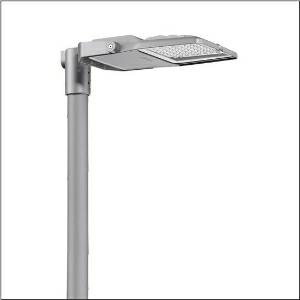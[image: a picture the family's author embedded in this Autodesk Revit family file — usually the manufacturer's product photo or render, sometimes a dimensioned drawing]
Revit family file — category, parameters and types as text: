
# Revit family: floodlight_fl_21_iq_mini___pl43_5xa7771b2a3a_6d21
name_source: partatom
category: Lighting Fixtures
units: mm (PartAtom-declared; Revit-internal decimal feet)

## family parameters
Cut with Voids When Loaded = No
Host = Face
Light Source = No
Part Type = Normal
Room Calculation Point = No
Round Connector Dimension = Use Diameter
Shared = No

## types (1)
- --- (1 x LED, 6400 lm, 45.5 W, 3000K)
    Apparent Load = 46 VA
    CIE Flux Codes = 27 78 99 100 100
    Color Rendering = 70
    Color Temperature = 3000K
    Default Elevation = 1800 mm
    Description = Floodlight FL 21 iQ mini, floodlight, primary light control with lens, of PMMA, primary optical cover: protective disc, of toughened safety glass, transparent, light distribution: PL43, light emission: direct distribution, installation type: surface-mounted, LED, High Power LED, rated luminous flux: 6.400lm, luminous efficacy: 141lm/W, light colour: 730, colour temperature: 3000K, control gear: iQ Comfort/DALI, control: Auto-Match, Temp-Guard, Lumen-Switch, Night-Set, Smart-Wire, Light-Fading, Desk-Remote (wireless, voltage-free reading and setting of iQ features in the workshop via application-optimized NFC function/RFID function), optimised constant luminous flux control (CLO 2.0), with terminal, 6-pole, mains connection: 220..240V, AC, 50/60Hz, start of lifetime: 46W, end of service life: 48W, reduction: 22W, luminaire housing, of diecast aluminium, powder-coated, Siteco® metallic grey (DB 702S), corrosivity category C5 mid according to DIN EN ISO 12944, suitable for swimming pools, chlorine-resistant, sealing non-destructively replaceable, please order mast flange separately, mast bracket, of steel, galvanised, powder-coated, Siteco® metallic grey (DB 702S), protection rating (complete): IP66, insulation class (complete): insulation class II (safety insulation), certification: CE, ENEC, VDE, protection symbol: D, impact resistance: IK08, permissible operating ambient temperature: -40..+40°C, permissible operating ambient temperature for outdoor applications: -40..+50°C, standard: DIN EN 12944, LABS conformity tested according to VDMA 24364:2018-05, packaging unit: 1 piece

Light Distribution: PL43
    Height = 70 mm
    Lamp = 1 x LED
    Lamp Light Flux = 6400 lm
    Lamp Power = 45.5 W
    Lamp count = 1
    Length = 485 mm
    Luminous efficacy = 141 lm/W
    Manufacturer = Siteco
    ModVariant = No
    Model = 5XA7771B2A3A
    Number of Poles = 1
    OnlyDefault = Yes
    Power Factor = 1
    Product Name = Floodlight FL 21 iQ mini | PL43
    Product group = floodlight | pylon annexe
    ProductGroupID = 6201
    Protection Class = Protection class II
    Protection Degree = IP 66
    RLX_Detail_Level = 1
    RLX_Emergency_Light_Flux = 0 lm
    RLX_Emergency_Type = 0
    RLX_Emergency_Type_DB = No
    RlxData = <blob elided: 101289 chars, md5=c1dfa50c>
    Socket = socket
    Standby Power = 0 W
    System Light Flux = 6400 lm
    System Power = 46 W
    Type Comments = factory setting: luminous flux: 100 % | dim-lin: 254 | 463 mA
    Type Image = l_1007125.jpg
    URL = http://relux.com
    VarID = @adj_184455
    Voltage = 0 V
    Weight = 0.00 kg
    Width = 337 mm

## geometry (parser evidence)
native form markers: Blend x4, Sweep x11
no freeform markers — native parametric forms only
